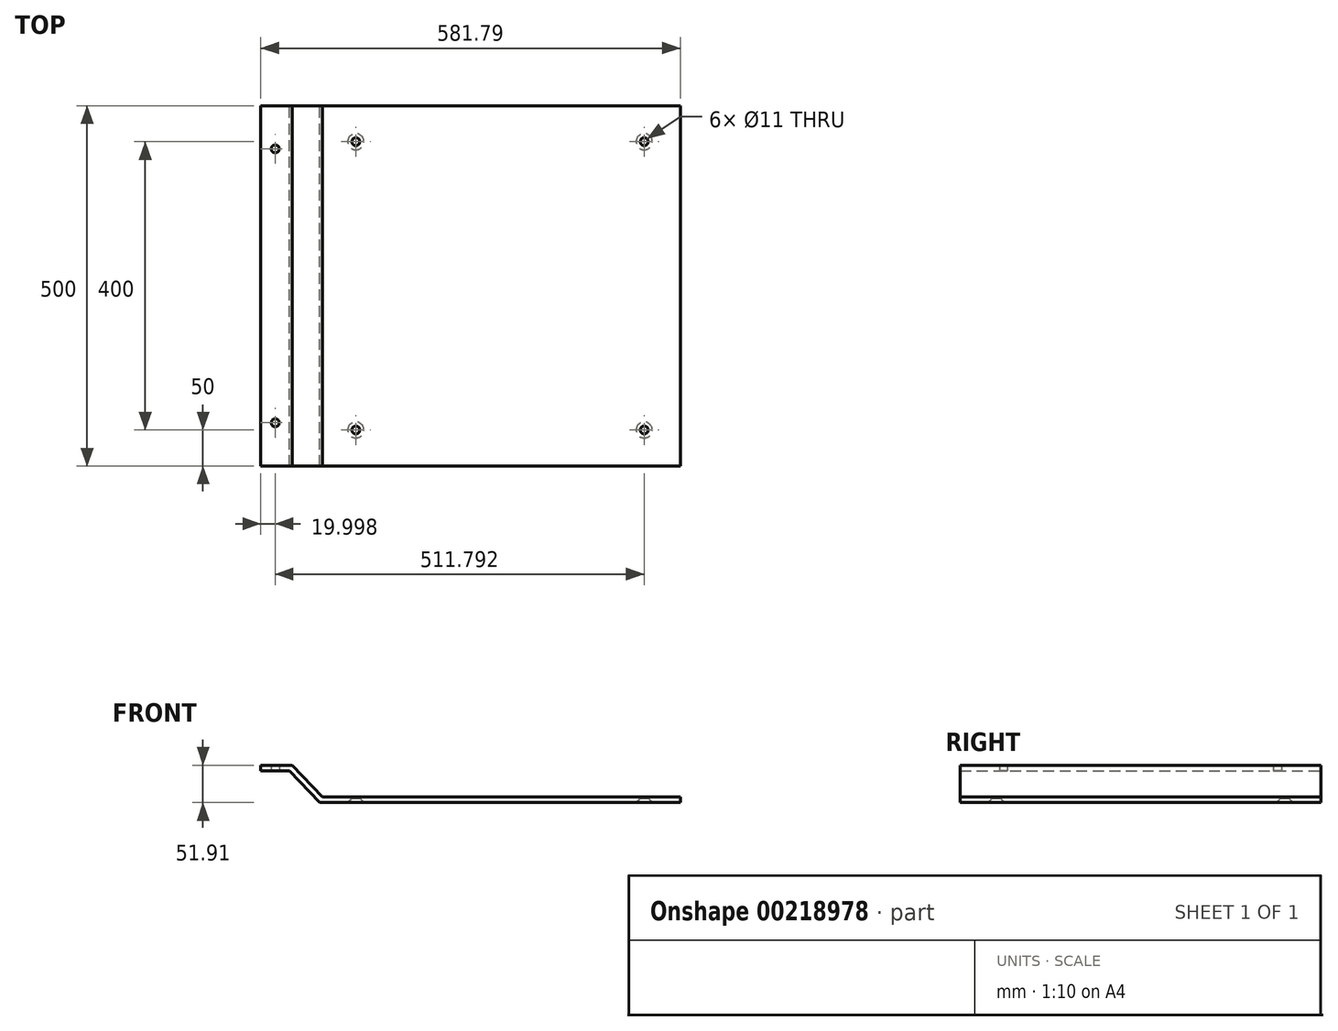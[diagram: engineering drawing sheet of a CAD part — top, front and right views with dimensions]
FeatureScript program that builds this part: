
annotation { "Feature Type Name" : "Feature", "Feature Type Description" : "" }
export const myFeature = defineFeature(function(context is Context, id is Id, definition is map)
    precondition{}
    {
        {
            var Q0;
            Q0=qCreatedBy(makeId("Front.planeOp"),FACE);
            var sketch = newSketch(context, id + "F0", { "sketchPlane" : qUnion([Q0])});
            skLineSegment(sketch, "E0", {"start": v(0, 0) * mm, "end": v(0, 8) * mm});
            skLineSegment(sketch, "E1", {"start": v(0, 8) * mm, "end": v(-496.57, 8) * mm});
            skLineSegment(sketch, "E2", {"start": v(0, 0) * mm, "end": v(-500, 0) * mm});
            skLineSegment(sketch, "E3", {"start": v(-500, 0) * mm, "end": v(-541.8, 43.9) * mm});
            skLineSegment(sketch, "E4", {"start": v(-520.9, 21.95) * mm, "end": v(-515.1, 27.47) * mm});
            skLineSegment(sketch, "E5", {"start": v(-541.8, 43.9) * mm, "end": v(-581.8, 43.9) * mm});
            skLineSegment(sketch, "E6", {"start": v(-581.8, 43.9) * mm, "end": v(-581.8, 51.9) * mm});
            skLineSegment(sketch, "E7", {"start": v(-581.8, 51.9) * mm, "end": v(-538.36, 51.9) * mm});
            skLineSegment(sketch, "E8", {"start": v(-538.36, 51.9) * mm, "end": v(-496.57, 8) * mm});
            skSolve(sketch);
        }
        {
            var Q0;
            {var subQ1=sQuery(id+"F0.wireOp",EDGE,"E4");Q0=makeQuery(id+"F0.imprint","IMPRINT",FACE,{"disambiguationData":[TD([[makeQuery(id+"F0.imprint","IMPRINT",EDGE,{"derivedFrom":subQ1}),1.0]])]});}
            var Q1;
            Q1=makeQuery(id+"F0.imprint","IMPRINT",FACE,{"disambiguationData":[TD([[makeQuery(id+"F0.imprint","IMPRINT",EDGE,{"derivedFrom":sQuery(id+"F0.wireOp",EDGE,"E0")}),1.0]])]});
            extrude(context, id + "F1", {"entities" : qUnion([Q0, Q1]), "endBound" : BoundingType.SYMMETRIC, "depth" : 500 * mm, "offsetDistance" : 25 * mm});
        }
        {
            var Q0;
            Q0=makeQuery(id+"F1.opExtrude","SWEPT_FACE",FACE,{"disambiguationData":[OSD([sQuery(id+"F0.wireOp",EDGE,"E2")])]});
            var sketch = newSketch(context, id + "F2", { "sketchPlane" : qUnion([Q0])});
            skPoint(sketch, "E9", {"position": v(-450, 200) * mm});
            skPoint(sketch, "E10", {"position": v(-50, 200) * mm});
            skPoint(sketch, "E11.MirrorP", {"position": v(-450, -200) * mm});
            skPoint(sketch, "E12.MirrorP", {"position": v(-50, -200) * mm});
            skSolve(sketch);
        }
        {
            var Q0;
            Q0=sQuery(id+"F2.wireOp",VERTEX,"E9");
            var Q1;
            Q1=sQuery(id+"F2.wireOp",VERTEX,"E10");
            var Q2;
            Q2=sQuery(id+"F2.wireOp",VERTEX,"E12.MirrorP");
            var Q3;
            Q3=sQuery(id+"F2.wireOp",VERTEX,"E11.MirrorP");
            var Q4;
            Q4=makeQuery(id+"F1.opExtrude","SWEPT_BODY",BODY,{"disambiguationData":[OSD([sQuery(id+"F0.wireOp",EDGE,"E0"),sQuery(id+"F0.wireOp",EDGE,"E1"),sQuery(id+"F0.wireOp",EDGE,"E2"),sQuery(id+"F0.wireOp",EDGE,"E3"),sQuery(id+"F0.wireOp",EDGE,"E5"),sQuery(id+"F0.wireOp",EDGE,"E6"),sQuery(id+"F0.wireOp",EDGE,"E7"),sQuery(id+"F0.wireOp",EDGE,"E8")])]});
            hole(context, id + "F3", {"style" : HoleStyle.C_SINK, "endStyle" : HoleEndStyle.THROUGH, "standardTappedOrClearance" : lookupTablePath({ "standard" : "ISO", "fit" : "Normal", "size" : "M10", "type" : "Clearance" }), "standardBlindInLast" : lookupTablePath({ "fit" : "Standard", "standard" : "ISO", "size" : "M10", "type" : "Clearance" }), "holeDiameter" : 11 * mm, "cSinkDiameter" : 22.4 * mm, "cSinkAngle" : 90 * degree, "majorDiameter" : 5 * mm, "isTappedThrough" : true, "tappedDepth" : 12 * mm, "tapClearance" : 3, "locations" : qUnion([Q0, Q1, Q2, Q3]), "scope" : qUnion([Q4])});
        }
        {
            var Q0;
            Q0=makeQuery(id+"F1.opExtrude","SWEPT_FACE",FACE,{"disambiguationData":[OSD([sQuery(id+"F0.wireOp",EDGE,"E5")])]});
            var sketch = newSketch(context, id + "F4", { "sketchPlane" : qUnion([Q0])});
            skPoint(sketch, "E13", {"position": v(-561.8, 190) * mm});
            skPoint(sketch, "E14.MirrorP", {"position": v(-561.8, -190) * mm});
            skSolve(sketch);
        }
        {
            var Q0;
            Q0=sQuery(id+"F4.wireOp",VERTEX,"E13");
            var Q1;
            Q1=sQuery(id+"F4.wireOp",VERTEX,"E14.MirrorP");
            var Q2;
            Q2=makeQuery(id+"F1.opExtrude","SWEPT_BODY",BODY,{"disambiguationData":[OSD([sQuery(id+"F0.wireOp",EDGE,"E0"),sQuery(id+"F0.wireOp",EDGE,"E1"),sQuery(id+"F0.wireOp",EDGE,"E2"),sQuery(id+"F0.wireOp",EDGE,"E3"),sQuery(id+"F0.wireOp",EDGE,"E5"),sQuery(id+"F0.wireOp",EDGE,"E6"),sQuery(id+"F0.wireOp",EDGE,"E7"),sQuery(id+"F0.wireOp",EDGE,"E8")])]});
            hole(context, id + "F5", {"style" : HoleStyle.SIMPLE, "endStyle" : HoleEndStyle.THROUGH, "standardTappedOrClearance" : lookupTablePath({ "standard" : "ISO", "fit" : "Normal", "size" : "M10", "type" : "Clearance" }), "standardBlindInLast" : lookupTablePath({ "fit" : "Standard", "standard" : "ISO", "size" : "M10", "type" : "Clearance" }), "holeDiameter" : 11 * mm, "majorDiameter" : 5 * mm, "isTappedThrough" : true, "tappedDepth" : 12 * mm, "tapClearance" : 3, "locations" : qUnion([Q0, Q1]), "scope" : qUnion([Q2])});
        }
    });
